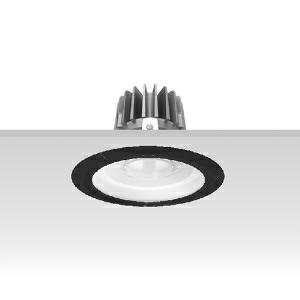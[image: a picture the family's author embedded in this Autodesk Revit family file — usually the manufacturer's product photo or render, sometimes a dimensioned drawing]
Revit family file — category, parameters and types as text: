
# Revit family: 3f_filippi_-_3f_reno_bianco_ampio_3f_filippi_-_30375_a01024_-_3f_reno_150_wh_2000-840_dali_wide___vt_bk_6c26
name_source: partatom
category: Lighting Fixtures
units: mm (PartAtom-declared; Revit-internal decimal feet)

## family parameters
Cut with Voids When Loaded = No
Host = Face
Light Source = No
Part Type = Normal
Room Calculation Point = No
Round Connector Dimension = Use Diameter
Shared = No

## types (1)
- 3F Filippi - 3F Reno Bianco Ampio (1 x LED, 1972 lm, 20 W, 4000 K)
    Apparent Load = 20 VA
    Approval mark = CE
    CIE Flux Codes = 74 93 99 100 100
    Color Rendering = 80
    Color Temperature = 4000 K
    Control Gear = Electronic transformer
    Default Elevation = 1800 mm
    Description = ILLUMINOTECHNICAL
Luminous efficiency 100% (DLOR 100%, ULOR 0%).
Initial luminous flux of the luminaire 1972 lm.
Direct symmetric wide distribution.
Installation Interdistance Transv.D = 1.54 x hu - Long.D = 1.54 x hu.
Tabular UGR (CIE 117 - 4H-8H; S=0.25H; 70/50/20): RUG 23.3 - 23.2.
Beam angle: 74° - 73°.
Luminous efficacy 99 lm/W.
Lifetime (L90/B10): 30000 h. (tq+25°C)
Lifetime (L85/B10): 50000 h. (tq+25°C)
Lifetime (L70/B10): 80000 h. (tq+25°C)
Sudden decreased luminous flux after 50000 hours: 0% (C0).
Photobiological safety in compliance with IEC/TR 62778: RG0 risk exempt, (IEC 62471).
In compliance with IEC/EN 62722-2-1 - IEC/EN 62717 standards.

SOURCE
Compact LED module 2000/840.
Energy efficiency class (UE 2019/2020 - UE 2019/2015): D.
CIE 13.3 Colour rendering index: CRI >80 (R9 <50%).
IES TM-30 Fidelity Index: Rf = 84 Rg = 95.
CCT nominal colour temperature 4000 K.
Colour initial tolerance (MacAdam): SDCM 3.
Zhaga Book 3 compliant.

MECHANICAL
Passive heat dissipator in die-casting aluminium, oversized, for optimum thermal management of the LED module.
Parabolic element with graduated/concentric rings in white polycarbonate.
Transparent external lens with glossy and satin differentiated surfaces, with a cooling and anti-insect system in methacrylate (PMMA).
Fastening spring clips in stainless steel.
Dimensions: diameter 176 mm, height 111 mm. Weight 0.84 kg.
IP44 protection degree for exposed part, IP20 for recessed part.
Mechanical strength to impacts IK06 (1 joule).
Glow-wire test resistance 650°C.

ELECTRICAL
Wiring on a separate unit.
Halogen Free DALI-2 DATI (Parts 251, 252, 253), PUSH-DIM, electronic wiring 230V-50/60Hz, power factor 0.90 at full load, THD <25%, constant output current, SELV, class II, 1 driver, 1 DALI addresse.
Power of the luminaire 20 W.
ENEC - CE.
SAFE FLICKER: PstLM=<1 and SVM=<0.4 (IEC TR 61547-1 and IEC TR 63158), to ensure a more comfortable and safe light.
Luminaire compliant with EN 60598-2-22 for power supply from a centralised emergency system CPSS (Central Power Supply System), not incorporated in the luminaire - high risk areas excluded. The default power and flux are 100% in AC and 100% in DC.
Ambient temperature from 0°C to +25°C.
Temperature class T6 max 85°C.
Relative humidity UR: <85%.

INSTALLATION
Pull-up recessed fitting.
False ceiling carving: 150 mm.
All accessories dedicated to this product are available on the Catalog and on our website www.3F-Filippi.com.

ACCESSORIES
A01024 - VT transparent glass, tempered, not flammable, locked and in line with the trim, in black polycarbonate.

APPLICATIONS
Environments: architectural, commercial, exhibition areas, transit areas, corridors, shops, display windows, service areas.
In false ceilings with narrow voids.

LIGHT MANAGEMENT
Recommended minimum setting: 10%.
The luminaire, equipped with (DALI-2 DATI) driver, can be controlled manually with 3F Easy Dim technology or automatically/manually with wired or wireless DALI/D2D control systems.
The D2D driver guarantees interoperability with other devices with the same certification by making the following information available:
Device Data (Part 251), Energy Report (Part 252), Diagnosis & Maintenance (Part 253).
In electrical systems without a regulation system (manual or automatic) and DALI bus, a suitable jumper must be made on the DA-DA terminals of the appliance.

WARNING
Luminaire designed for disposal/recycling at end-of-life.
Replaceable (LED only) light source by a professional. Replaceable control gear by a professional.
    Height = 0 mm  [stored 0 ft]
    Lamp = 1 x LED
    Lamp Light Flux = 1972 lm
    Lamp Power = 20 W
    Lamp count = 1
    Length = 176 mm
    Lifetime = 50000 h
    Luminous efficacy = 99 lm/W
    Manufacturer = 3F Filippi
    ModVariant = No
    Model = 3F Filippi - 30375+A01024 - 3F Reno 150 WH 2000-840 DALI WIDE + VT BK
    Mounting Place = Ceiling
    Mounting Type = Recessed
    Number of Poles = 1
    OnlyDefault = Yes
    Power Factor = 1
    Product Name = 3F Filippi - 3F Reno Bianco Ampio
    Product group = recessed luminaire
    ProductGroupID = 4
    Protection Class = Protection class II
    Protection Degree = IP 20
    RLX_Detail_Level = 1
    RLX_Emergency_Light_Flux = 0 lm
    RLX_Emergency_Type = 0
    RLX_Emergency_Type_DB = No
    RlxData = <blob elided: 87257 chars, md5=48a794cf>
    Socket = socket
    Standby Power = 0 W
    System Light Flux = 1972 lm
    System Power = 20 W
    Type Comments = Product without accessories
    Type Image = 3ffilippi_3f_reno_150_wh_d100__a01024.jpg
    URL = http://relux.com
    VarID = ---
    Voltage = 0 V
    Weight = 0.00 kg
    Width = 0 mm  [stored 0 ft]

note: [stored X ft] marks values corroborated as IEEE doubles in the binary element streams (Revit-internal decimal feet)

## geometry (parser evidence)
native form markers: Blend x4, Sweep x12
no freeform markers — native parametric forms only
